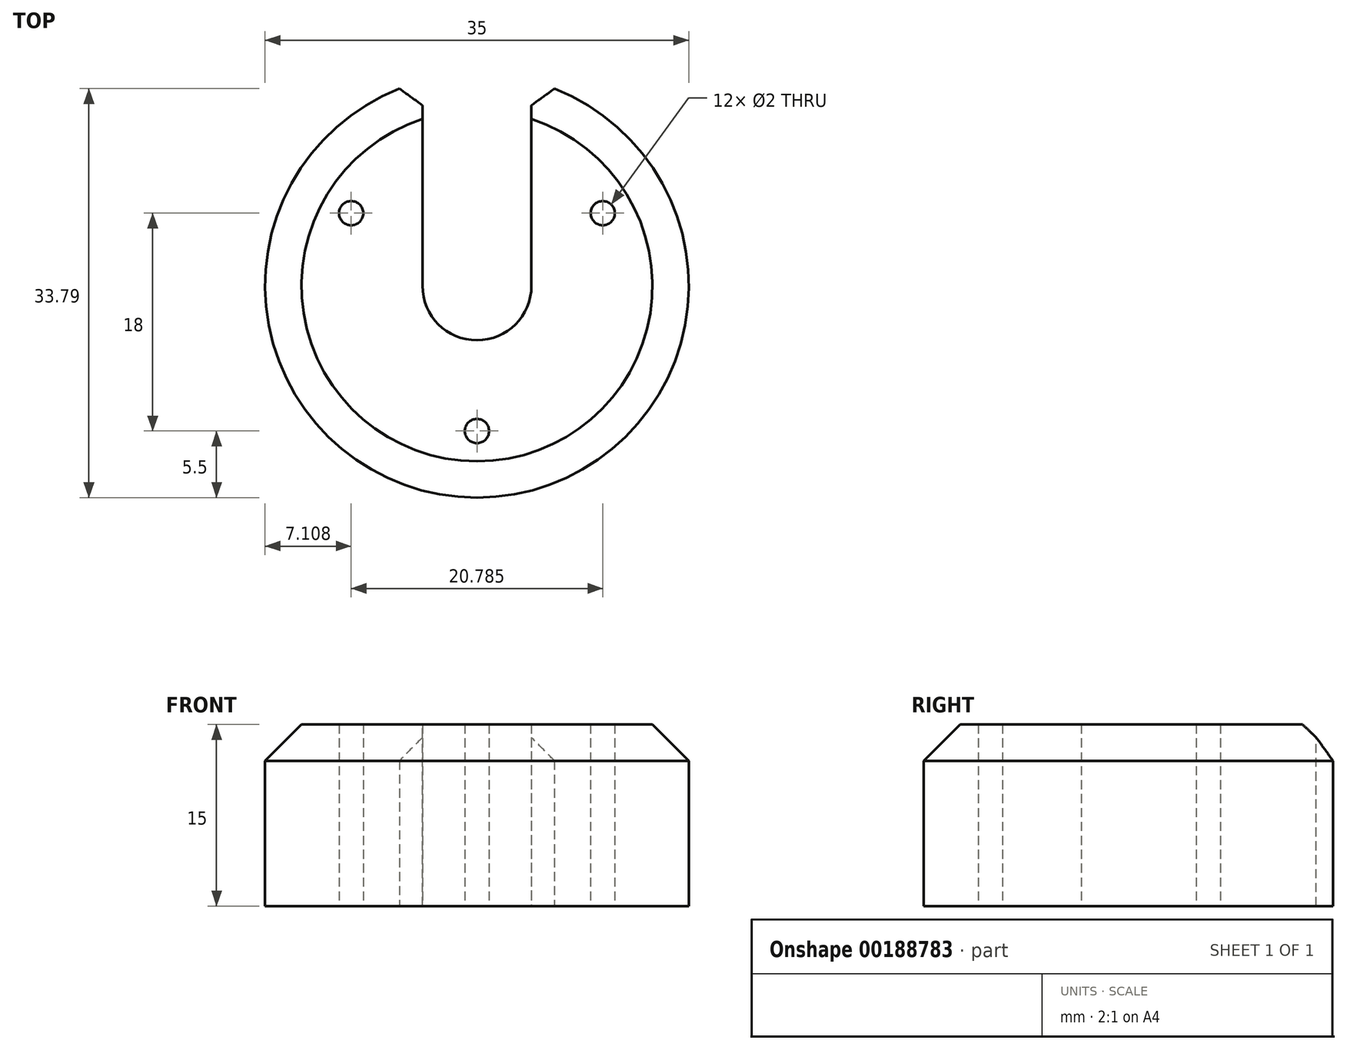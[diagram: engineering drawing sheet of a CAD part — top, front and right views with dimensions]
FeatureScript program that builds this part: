
annotation { "Feature Type Name" : "Feature", "Feature Type Description" : "" }
export const myFeature = defineFeature(function(context is Context, id is Id, definition is map)
    precondition{}
    {
        {
            var Q0;
            Q0=qCreatedBy(makeId("Top.planeOp"),FACE);
            var sketch = newSketch(context, id + "F0", { "sketchPlane" : qUnion([Q0])});
            skCircle(sketch, "E0", {"center": v(0, 0) * mm, "radius": 17.5 * mm});
            skCircle(sketch, "E1", {"center": v(0, 0) * mm, "radius": 4.5 * mm});
            skLineSegment(sketch, "E2", {"start": v(4.5, 0) * mm, "end": v(4.5, 16.91) * mm});
            skLineSegment(sketch, "E3", {"start": v(-4.5, 0) * mm, "end": v(-4.5, 16.91) * mm});
            skLineSegment(sketch, "E4", {"start": v(0, 0) * mm, "end": v(0, -17.5) * mm, "construction": true});
            skLineSegment(sketch, "E5", {"start": v(0, 0) * mm, "end": v(-15.16, 8.75) * mm, "construction": true});
            skCircle(sketch, "E6", {"center": v(0, -12) * mm, "radius": 1 * mm});
            skCircle(sketch, "E7.1.0", {"center": v(-10.4, 6) * mm, "radius": 1 * mm});
            skCircle(sketch, "E7.2.0", {"center": v(10.4, 6) * mm, "radius": 1 * mm});
            skLineSegment(sketch, "E8", {"start": v(0, 0) * mm, "end": v(10.4, 6) * mm, "construction": true});
            skSolve(sketch);
        }
        {
            var Q0;
            {var subQ1=sQuery(id+"F0.wireOp",EDGE,"E2");Q0=makeQuery(id+"F0.imprint","IMPRINT",FACE,{"disambiguationData":[TD([[makeQuery(id+"F0.imprint","IMPRINT",EDGE,{"derivedFrom":subQ1}),-1.0]])]});}
            extrude(context, id + "F1", {"entities" : qUnion([Q0]), "depth" : 15 * mm});
        }
        {
            var Q0;
            Q0=makeQuery(id+"F1.opExtrude","CAP_EDGE",EDGE,{"disambiguationData":[OSD([sQuery(id+"F0.wireOp",EDGE,"E0")])],"isStart":false});
            chamfer(context, id + "F2", {"entities" : qUnion([Q0]), "width" : 3 * mm, "tangentPropagation" : true});
        }
        {
            var Q0;
            Q0=makeQuery(id+"F1.opExtrude","SWEPT_EDGE",EDGE,{"disambiguationData":[OSD([sQuery(id+"F0.wireOp",EDGE,"E0"),sQuery(id+"F0.wireOp",EDGE,"E3")])]});
            var Q1;
            Q1=makeQuery(id+"F1.opExtrude","SWEPT_EDGE",EDGE,{"disambiguationData":[OSD([sQuery(id+"F0.wireOp",EDGE,"E0"),sQuery(id+"F0.wireOp",EDGE,"E2")])]});
            chamfer(context, id + "F3", {"entities" : qUnion([Q0, Q1]), "width" : 2 * mm, "tangentPropagation" : true});
        }
    });
